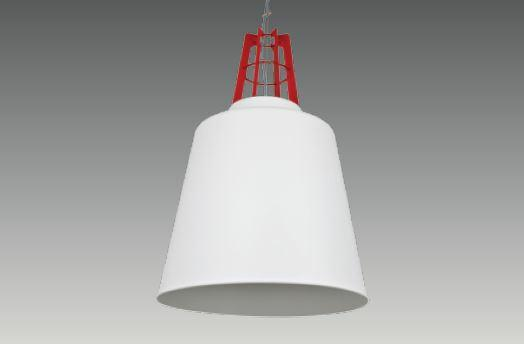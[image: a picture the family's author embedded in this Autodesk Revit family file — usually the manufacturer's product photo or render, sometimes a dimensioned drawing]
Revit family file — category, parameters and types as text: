
# Revit family: S 0500 DEF-9
name_source: partatom
category: Lighting Fixtures
revit_build: Autodesk Revit 2016 (Build: 20150714_1515(x64)
units: mm (PartAtom-declared; Revit-internal decimal feet)

## family parameters
Cut with Voids When Loaded = No
Host = Face
Light Source = Yes
Part Type = Normal
Room Calculation Point = No
Round Connector Dimension = Use Diameter
Shared = No

## types (2) — shared parameters
Color Filter = 16777215
Default Elevation = 1219 mm
Dimming Lamp Color Temperature Shift = <None>
Emit Shape Visible in Rendering = Yes
Emit from Circle Diameter = 490 mm  [stored 1.60761 ft]
Light Source Symbol Size = 610 mm
Manufacturer = ARLIGHT
Type Image = S 0500 DEF.JPG
Wattage Comments = 32

## type names (no varying parameters)
- SDEF.500.32.30
- SDEF.500.32.40

note: [stored X ft] marks values corroborated as IEEE doubles in the binary element streams (Revit-internal decimal feet)

## geometry (parser evidence)
native form markers: Sweep x3
no freeform markers — native parametric forms only
